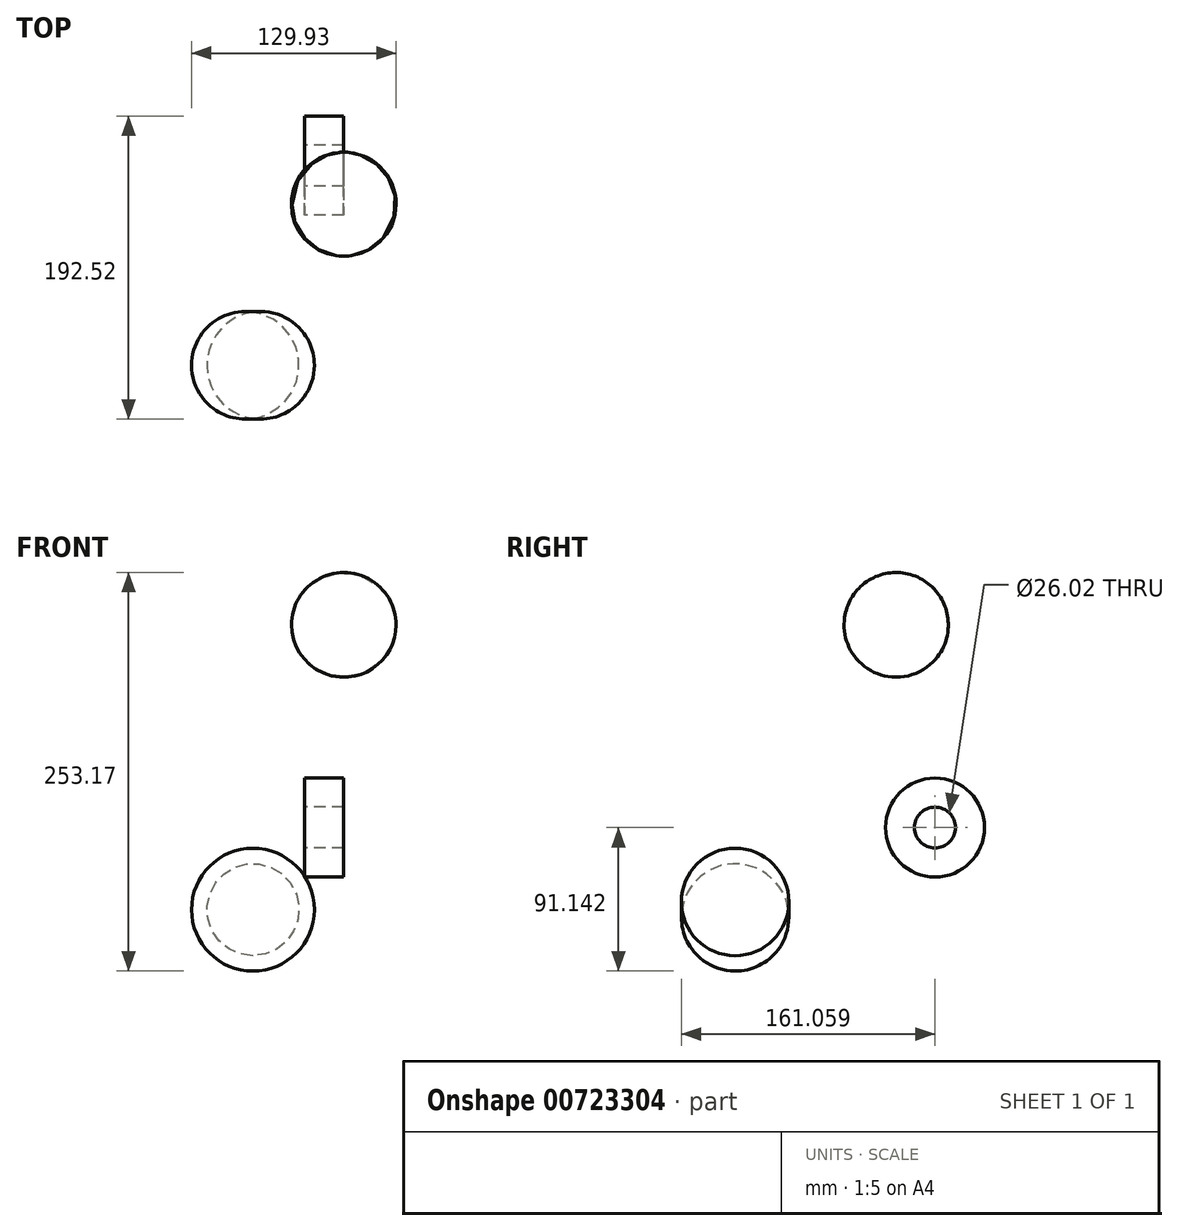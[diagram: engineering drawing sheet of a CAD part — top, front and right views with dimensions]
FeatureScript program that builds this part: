
annotation { "Feature Type Name" : "Feature", "Feature Type Description" : "" }
export const myFeature = defineFeature(function(context is Context, id is Id, definition is map)
    precondition{}
    {
        {
            var Q0;
            Q0=qCreatedBy(makeId("Top.planeOp"),FACE);
            var sketch = newSketch(context, id + "F0", { "sketchPlane" : qUnion([Q0])});
            skLineSegment(sketch, "E0", {"start": v(-32.68, 38.1) * mm, "end": v(-32.68, -29.43) * mm});
            skArc(sketch, "E1", {"start": v(-32.68, -29.43) * mm, "mid": v(-3.45, 4.34) * mm, "end": v(-32.68, 38.1) * mm});
            skSolve(sketch);
        }
        {
            var Q0;
            Q0=makeQuery(id+"F0.imprint","IMPRINT",FACE,{"disambiguationData":[TD([[makeQuery(id+"F0.imprint","IMPRINT",EDGE,{"derivedFrom":sQuery(id+"F0.wireOp",EDGE,"E0")}),1.0]])]});
            var Q1;
            Q1=sQuery(id+"F0.wireOp",EDGE,"E0");
            revolve(context, id + "F1", {"surfaceOperationType" : NewSurfaceOperationType.NEW, "entities" : qUnion([Q0]), "axis" : qUnion([Q1]), "revolveType" : RevolveType.FULL});
        }
        {
            var Q0;
            Q0=qCreatedBy(makeId("Right.planeOp"),FACE);
            var sketch = newSketch(context, id + "F2", { "sketchPlane" : qUnion([Q0])});
            skCircle(sketch, "E2", {"center": v(131.28, 52.14) * mm, "radius": 31.46 * mm});
            skCircle(sketch, "E3", {"center": v(131.28, 52.14) * mm, "radius": 13 * mm});
            skSolve(sketch);
        }
        {
            var Q0;
            Q0 = qSketchRegion(id + "F2", true);
            extrude(context, id + "F3", {"entities" : qUnion([Q0]), "depth" : 25 * mm, "offsetDistance" : 25 * mm});
        }
        {
            var Q0;
            Q0=makeQuery(id+"F3.opExtrude","CAP_FACE",FACE,{"disambiguationData":[OSD([sQuery(id+"F2.wireOp",EDGE,"E2"),sQuery(id+"F2.wireOp",EDGE,"E3")])],"isStart":false});
            var sketch = newSketch(context, id + "F4", { "sketchPlane" : qUnion([Q0])});
            skLineSegment(sketch, "E4", {"start": v(139.58, 178.16) * mm, "end": v(73.68, 183.68) * mm});
            skArc(sketch, "E5", {"start": v(73.68, 183.68) * mm, "mid": v(103.89, 148.16) * mm, "end": v(139.58, 178.16) * mm});
            skSolve(sketch);
        }
        {
            var Q0;
            Q0=makeQuery(id+"F4.imprint","IMPRINT",FACE,{"disambiguationData":[TD([[makeQuery(id+"F4.imprint","IMPRINT",EDGE,{"derivedFrom":sQuery(id+"F4.wireOp",EDGE,"E4")}),1.0]])]});
            var Q1;
            Q1=sQuery(id+"F4.wireOp",EDGE,"E4");
            revolve(context, id + "F5", {"surfaceOperationType" : NewSurfaceOperationType.NEW, "entities" : qUnion([Q0]), "axis" : qUnion([Q1]), "revolveType" : RevolveType.FULL});
        }
    });
